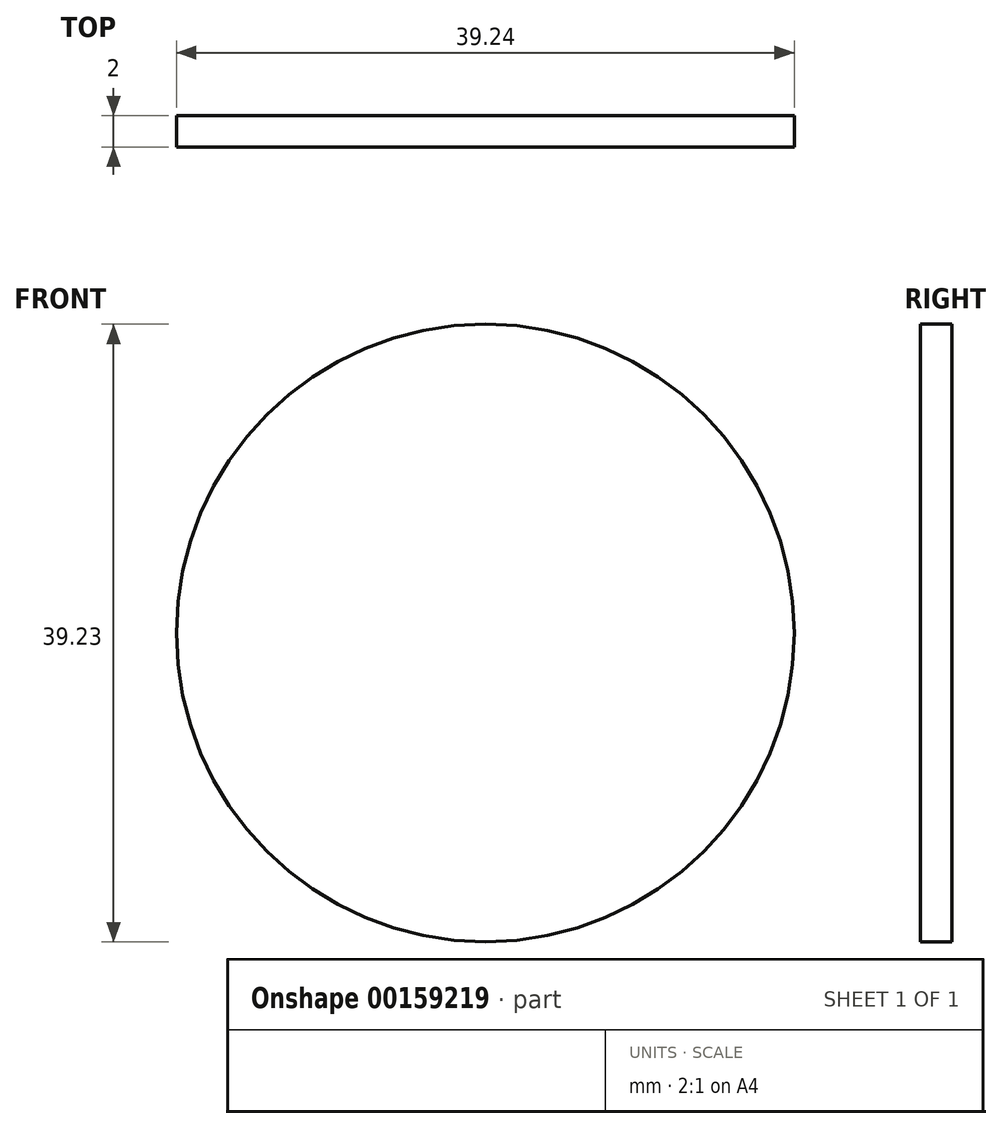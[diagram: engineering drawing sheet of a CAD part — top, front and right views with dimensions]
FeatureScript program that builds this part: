
annotation { "Feature Type Name" : "Feature", "Feature Type Description" : "" }
export const myFeature = defineFeature(function(context is Context, id is Id, definition is map)
    precondition{}
    {
        {
            var Q0;
            Q0=qCreatedBy(makeId("Front.planeOp"),FACE);
            var sketch = newSketch(context, id + "F0", { "sketchPlane" : qUnion([Q0])});
            skCircle(sketch, "E0", {"center": v(-1.9, 25.39) * mm, "radius": 19.62 * mm});
            skSolve(sketch);
        }
        {
            var Q0;
            Q0=makeQuery(id+"F0.imprint","IMPRINT",FACE,{"disambiguationData":[TD([[makeQuery(id+"F0.imprint","IMPRINT",EDGE,{"derivedFrom":sQuery(id+"F0.wireOp",EDGE,"E0")}),1.0]])]});
            extrude(context, id + "F1", {"entities" : qUnion([Q0]), "depth" : 2 * mm});
        }
    });
